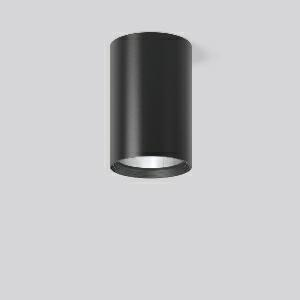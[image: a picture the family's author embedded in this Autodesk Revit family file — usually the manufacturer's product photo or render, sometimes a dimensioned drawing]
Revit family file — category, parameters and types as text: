
# Revit family: heledon_maxi_a_931239_003_7413
name_source: partatom
category: Lighting Fixtures
units: mm (PartAtom-declared; Revit-internal decimal feet)

## family parameters
Cut with Voids When Loaded = No
Host = Face
Light Source = No
Part Type = Normal
Room Calculation Point = No
Round Connector Dimension = Use Diameter
Shared = No

## types (1)
- HELEDON maxi A (1 x LED Modul 920 meat+, 2250 lm, 2000)
    Apparent Load = 33 VA
    Approval mark = CE
    CIE Flux Codes = 100 100 100 100 100
    Color Rendering = 90
    Color Temperature = 2000
    Default Elevation = 1800 mm
    Description = Series: HELEDON maxi
Cylindrical surface-mounted downlight. Housing: die-cast aluminium, powder-coated. Internal ceiling frame polycarbonate with bayonet mounting. Black plastic ring and recessed LED to prevent glare from the side. Optical assembly with reflector made of MIRO-Silver with 98% total light reflection for outstanding efficiency - can be changed without tools. Special LED for illumination of meat included. Suitable for Ceiling mounting. Easy installation with a separate ceiling frame with bayonet mounting and plug connection. Driver integrated. Connected via plug-in connector. High quality converter without flickering and stroboscopic effect. The following accessories can be mounted without use of tools: interchangeable lenses, decorative glasses, honeycomb louvre, clear and frosted diffusers, white interchangeable plastic ring. 
Colour: deep black, matt (RAL 9005)
Diameter: 123 mm
Height: 183 mm
Lamp: LED
Socket: without socket
Colour temperature: meat +
System power: 33 W
Rated luminous flux: 2250 lm
Luminous efficiency: 68 lm/W
Control gear: Regulated power supply
Protection class: I
Type of protection: IP 20
    Height = 183 mm
    Lamp = 1 x LED Modul 920 meat+
    Lamp Light Flux = 2250 lm
    Lamp count = 1
    Length = 123 mm
    Lifetime = 50000 h
    Luminous efficacy = 68 lm/W
    Manufacturer = RZB
    ModVariant = No
    Model = 931239.003
    Mounting Place = Ceiling
    Mounting Type = Surface mounted
    Number of Poles = 1
    OnlyDefault = Yes
    Power Factor = 1
    Product Name = HELEDON maxi A
    Product group = Surface mounted downlights
    ProductGroupID = 302
    Protection Class = Protection class I
    Protection Degree = IP 20
    RLX_Detail_Level = 1
    RLX_Emergency_Light_Flux = 0 lm
    RLX_Emergency_Type = 0
    RLX_Emergency_Type_DB = No
    RlxData = <blob elided: 96969 chars, md5=c756adbb>
    Socket = socket
    Standby Power = 0 W
    System Light Flux = 2250 lm
    System Power = 33 W
    Type Comments = Product without accessories
    Type Image = 931192.003.jpg
    URL = http://relux.com
    VarID = ---
    Voltage = 230 V
    Voltage Range = 220-240 V
    Weight = 0.00 kg
    Width = 0 mm  [stored 0 ft]

note: [stored X ft] marks values corroborated as IEEE doubles in the binary element streams (Revit-internal decimal feet)

## geometry (parser evidence)
native form markers: Blend x4, Sweep x11
no freeform markers — native parametric forms only
